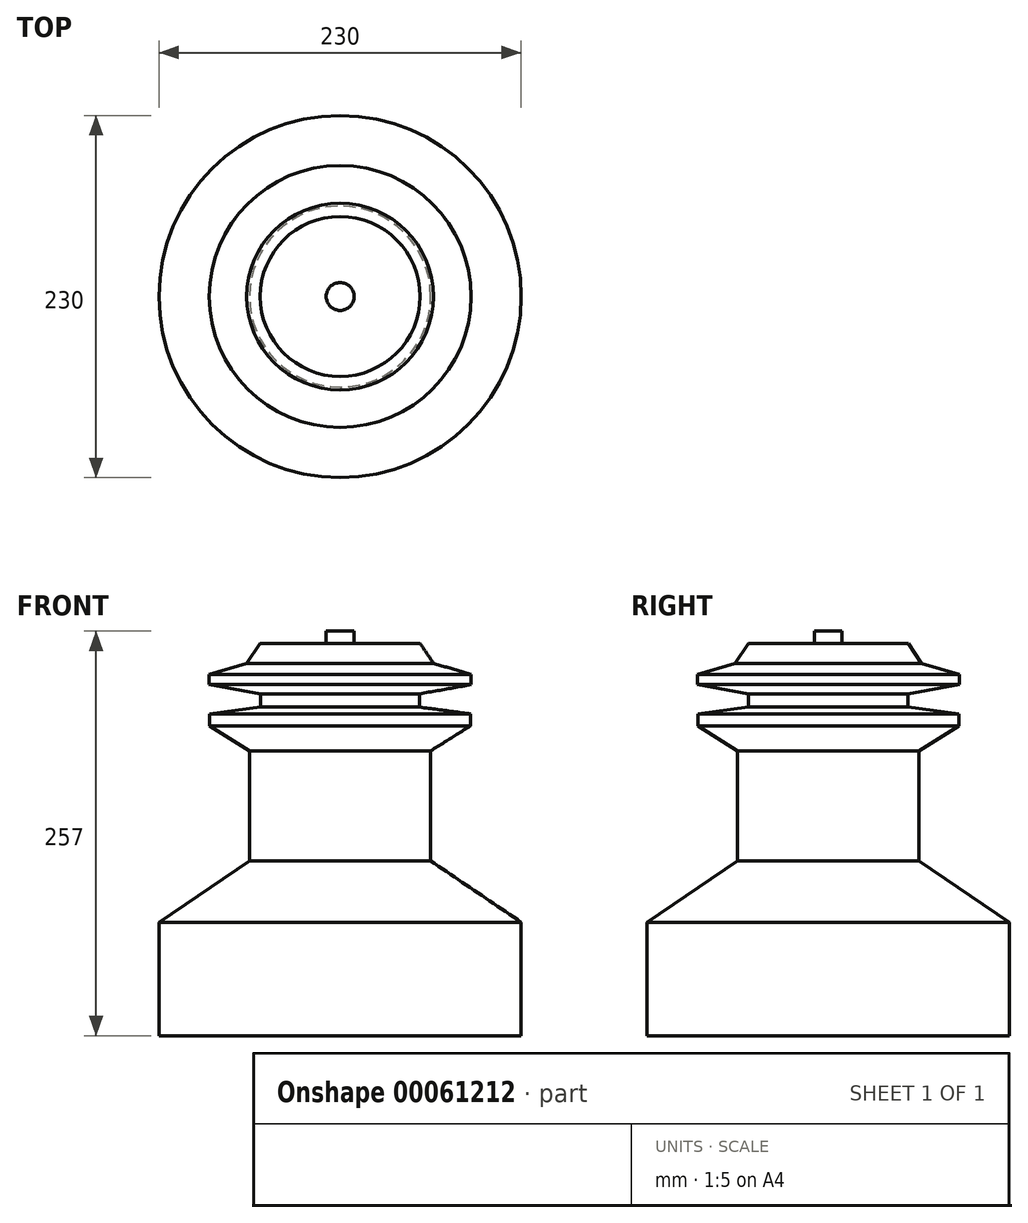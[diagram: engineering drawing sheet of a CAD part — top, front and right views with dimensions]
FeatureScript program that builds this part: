
annotation { "Feature Type Name" : "Feature", "Feature Type Description" : "" }
export const myFeature = defineFeature(function(context is Context, id is Id, definition is map)
    precondition{}
    {
        {
            var Q0;
            Q0=qCreatedBy(makeId("Front.planeOp"),FACE);
            var sketch = newSketch(context, id + "F0", { "sketchPlane" : qUnion([Q0])});
            skLineSegment(sketch, "E0", {"start": v(234, 343.23) * mm, "end": v(234, 0) * mm, "construction": true});
            skLineSegment(sketch, "E1", {"start": v(234, 297) * mm, "end": v(242.86, 297) * mm});
            skLineSegment(sketch, "E2", {"start": v(242.86, 297) * mm, "end": v(242.86, 289.25) * mm});
            skLineSegment(sketch, "E3", {"start": v(242.86, 289.25) * mm, "end": v(284.78, 289.25) * mm});
            skLineSegment(sketch, "E4", {"start": v(284.78, 289.25) * mm, "end": v(293.27, 276.51) * mm});
            skLineSegment(sketch, "E5", {"start": v(293.27, 276.51) * mm, "end": v(317.17, 269.4) * mm});
            skLineSegment(sketch, "E6", {"start": v(317.17, 269.4) * mm, "end": v(317.17, 262.95) * mm});
            skLineSegment(sketch, "E7", {"start": v(317.17, 262.95) * mm, "end": v(284.55, 257.15) * mm});
            skLineSegment(sketch, "E8", {"start": v(284.55, 257.15) * mm, "end": v(284.55, 248.7) * mm});
            skLineSegment(sketch, "E9", {"start": v(284.55, 248.7) * mm, "end": v(316.85, 244.36) * mm});
            skLineSegment(sketch, "E10", {"start": v(316.85, 244.36) * mm, "end": v(316.85, 236.8) * mm});
            skLineSegment(sketch, "E11", {"start": v(316.85, 236.8) * mm, "end": v(291.5, 220.9) * mm});
            skLineSegment(sketch, "E12", {"start": v(291.5, 220.9) * mm, "end": v(291.5, 151) * mm});
            skLineSegment(sketch, "E13", {"start": v(291.5, 151) * mm, "end": v(349, 112.09) * mm});
            skLineSegment(sketch, "E14", {"start": v(349, 112.09) * mm, "end": v(349, 40) * mm});
            skLineSegment(sketch, "E15", {"start": v(349, 40) * mm, "end": v(234, 40) * mm});
            skLineSegment(sketch, "E16", {"start": v(234, 297) * mm, "end": v(234, 40) * mm});
            skLineSegment(sketch, "E17", {"start": v(234, 316.19) * mm, "end": v(494, 343.23) * mm});
            skLineSegment(sketch, "E18", {"start": v(494, 343.23) * mm, "end": v(494, 422.14) * mm});
            skLineSegment(sketch, "E19", {"start": v(494, 422.14) * mm, "end": v(534, 422.14) * mm});
            skLineSegment(sketch, "E20", {"start": v(534, 422.14) * mm, "end": v(534, 327.28) * mm});
            skLineSegment(sketch, "E21", {"start": v(534, 327.28) * mm, "end": v(242.86, 297) * mm});
            skLineSegment(sketch, "E22", {"start": v(234, 316.19) * mm, "end": v(234, 297) * mm});
            skSolve(sketch);
        }
        {
            var Q0;
            Q0=makeQuery(id+"F0.imprint","IMPRINT",FACE,{"disambiguationData":[TD([[makeQuery(id+"F0.imprint","IMPRINT",EDGE,{"derivedFrom":sQuery(id+"F0.wireOp",EDGE,"E1")}),-1.0]])]});
            var Q1;
            Q1=sQuery(id+"F0.wireOp",EDGE,"E0");
            revolve(context, id + "F1", {"entities" : qUnion([Q0]), "axis" : qUnion([Q1]), "revolveType" : RevolveType.FULL});
        }
        {
            var Q0;
            Q0=makeQuery(id+"F0.imprint","IMPRINT",FACE,{"disambiguationData":[TD([[makeQuery(id+"F0.imprint","IMPRINT",EDGE,{"derivedFrom":sQuery(id+"F0.wireOp",EDGE,"E1")}),1.0]])]});
            var Q1;
            Q1=sQuery(id+"F0.wireOp",EDGE,"E18");
            var Q2;
            Q2=sQuery(id+"F0.wireOp",EDGE,"E19");
            var Q3;
            Q3=sQuery(id+"F0.wireOp",EDGE,"E20");
            var Q4;
            Q4=sQuery(id+"F0.wireOp",EDGE,"E0");
            revolve(context, id + "F2", {"bodyType" : ToolBodyType.SURFACE, "operationType" : NewBodyOperationType.ADD, "entities" : qUnion([Q0]), "surfaceEntities" : qUnion([Q1, Q2, Q3]), "axis" : qUnion([Q4]), "revolveType" : RevolveType.FULL});
        }
    });
